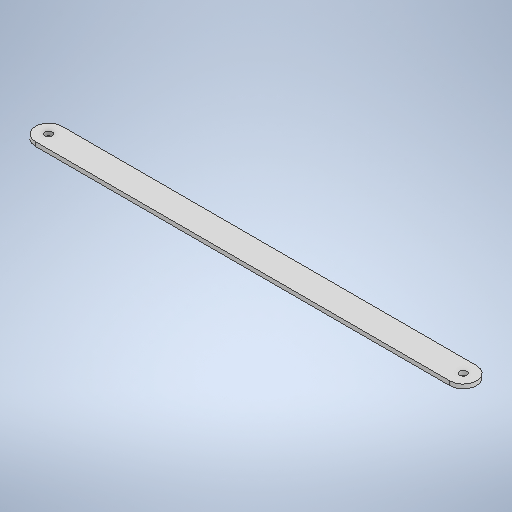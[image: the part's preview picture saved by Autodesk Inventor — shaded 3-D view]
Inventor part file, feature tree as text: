
AUTODESK INVENTOR PART (.ipt)
format: ipt  version: 2025.2 (Build 292293000, 293)  size: 266,240 bytes
history: native  units: in
note: dims shown in document units (in); Inventor stores cm internally (conversion verified against a paired STEP export)
features: extrude x2, sketch x2
ambient origin geometry x8: Origin, YZ Plane, XZ Plane, XY Plane, X Axis, Y Axis, Z Axis, Center Point
bodies: Solid1 (feature_tree)
feature tree (4):
  extrude  "Extrusion1"  Depth=0.4295in
  extrude  "Extrusion2"  Depth=0.0669in TaperAngle=0.0deg
  sketch  "Sketch1"  dims[d0=0.4295in d1=0.4295in]
  sketch  "Sketch2"  dims[d2=6.6929in d3=0.0669in d4=0.0in d5=0.1181in d6=0.1181in d7=0.0669in d8=0.0in]
